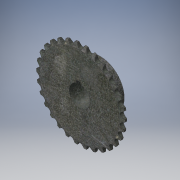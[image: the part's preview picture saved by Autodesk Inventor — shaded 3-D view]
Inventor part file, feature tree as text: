
AUTODESK INVENTOR PART (.ipt)
format: ipt  version: 2016 (Build 200138000, 138)  size: 1,100,288 bytes
history: native  units: in
note: dims shown in document units (in); Inventor stores cm internally (conversion verified against a paired STEP export)
features: plane x1, pattern_circular x1
ambient origin geometry x8: Origin, YZ Plane, XZ Plane, XY Plane, X Axis, Y Axis, Z Axis, Center Point
bodies: Solid1 (feature_tree)
feature tree (2):
  plane  "Work Plane1"
  pattern_circular  "CirPattern1"
